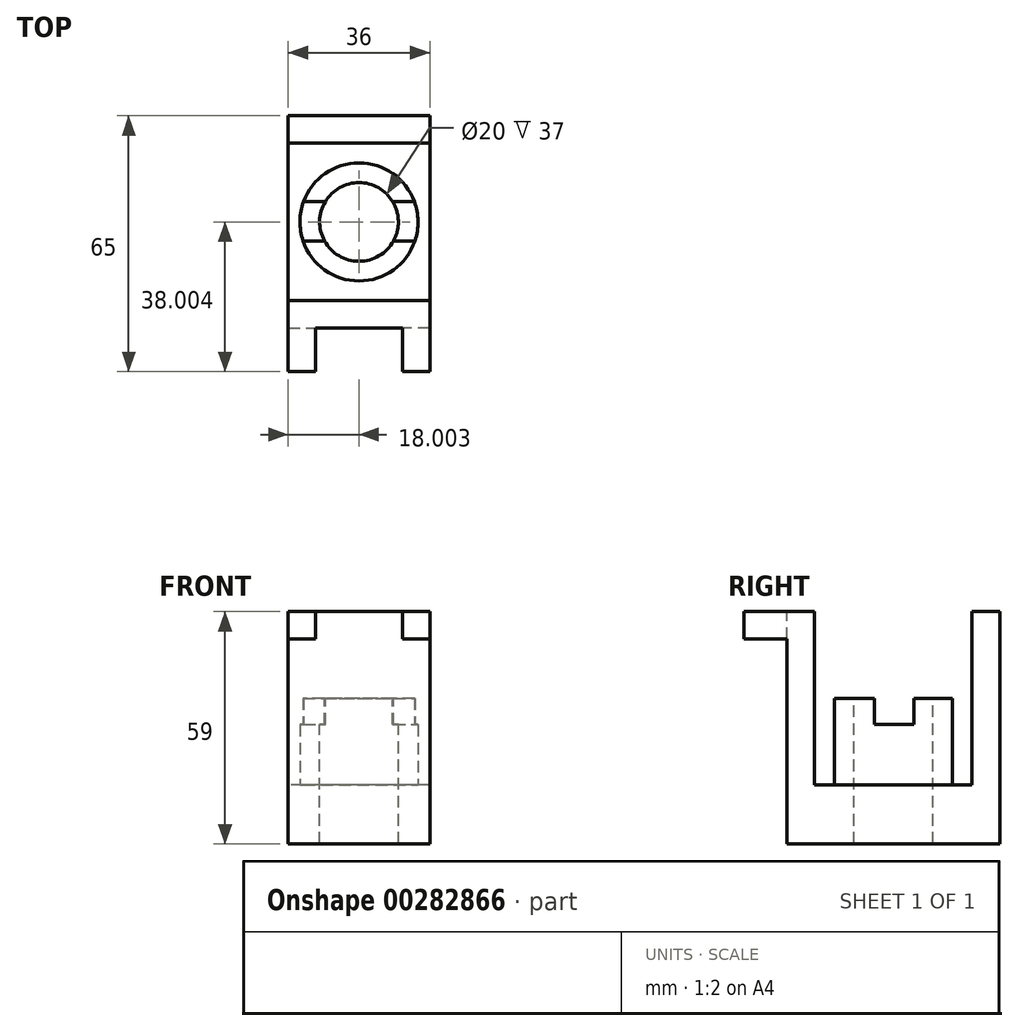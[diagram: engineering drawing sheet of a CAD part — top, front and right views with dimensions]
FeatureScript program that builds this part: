
annotation { "Feature Type Name" : "Feature", "Feature Type Description" : "" }
export const myFeature = defineFeature(function(context is Context, id is Id, definition is map)
    precondition{}
    {
        {
            var Q0;
            Q0=qCreatedBy(makeId("Top.planeOp"),FACE);
            var sketch = newSketch(context, id + "F0", { "sketchPlane" : qUnion([Q0])});
            skLineSegment(sketch, "E0.bottom", {"start": v(-73.88, -73.37) * mm, "end": v(-37.88, -73.37) * mm});
            skLineSegment(sketch, "E0.top", {"start": v(-73.88, -19.37) * mm, "end": v(-37.88, -19.37) * mm});
            skLineSegment(sketch, "E0.left", {"start": v(-73.88, -73.37) * mm, "end": v(-73.88, -19.37) * mm});
            skLineSegment(sketch, "E0.right", {"start": v(-37.88, -73.37) * mm, "end": v(-37.88, -19.37) * mm});
            skSolve(sketch);
        }
        {
            var Q0;
            Q0=makeQuery(id+"F0.imprint","IMPRINT",FACE,{"disambiguationData":[TD([[makeQuery(id+"F0.imprint","IMPRINT",EDGE,{"derivedFrom":sQuery(id+"F0.wireOp",EDGE,"E0.bottom")}),1.0]])]});
            extrude(context, id + "F1", {"entities" : qUnion([Q0]), "depth" : 15 * mm});
        }
        {
            var Q0;
            Q0=makeQuery(id+"F1.opExtrude","CAP_FACE",FACE,{"disambiguationData":[OSD([sQuery(id+"F0.wireOp",EDGE,"E0.bottom"),sQuery(id+"F0.wireOp",EDGE,"E0.top"),sQuery(id+"F0.wireOp",EDGE,"E0.left"),sQuery(id+"F0.wireOp",EDGE,"E0.right")])],"isStart":false});
            var sketch = newSketch(context, id + "F2", { "sketchPlane" : qUnion([Q0])});
            skLineSegment(sketch, "E1.bottom", {"start": v(-73.88, -19.37) * mm, "end": v(-37.88, -19.37) * mm});
            skLineSegment(sketch, "E1.top", {"start": v(-73.88, -26.37) * mm, "end": v(-37.88, -26.37) * mm});
            skLineSegment(sketch, "E1.left", {"start": v(-73.88, -19.37) * mm, "end": v(-73.88, -26.37) * mm});
            skLineSegment(sketch, "E1.right", {"start": v(-37.88, -19.37) * mm, "end": v(-37.88, -26.37) * mm});
            skLineSegment(sketch, "E2.bottom", {"start": v(-37.88, -73.37) * mm, "end": v(-73.88, -73.37) * mm});
            skLineSegment(sketch, "E2.top", {"start": v(-37.88, -66.37) * mm, "end": v(-73.88, -66.37) * mm});
            skLineSegment(sketch, "E2.left", {"start": v(-37.88, -73.37) * mm, "end": v(-37.88, -66.37) * mm});
            skLineSegment(sketch, "E2.right", {"start": v(-73.88, -73.37) * mm, "end": v(-73.88, -66.37) * mm});
            skSolve(sketch);
        }
        {
            var Q0;
            Q0=makeQuery(id+"F2.imprint","IMPRINT",FACE,{"disambiguationData":[TD([[makeQuery(id+"F2.imprint","IMPRINT",EDGE,{"derivedFrom":sQuery(id+"F2.wireOp",EDGE,"E1.bottom")}),-1.0]])]});
            var Q1;
            Q1=makeQuery(id+"F2.imprint","IMPRINT",FACE,{"disambiguationData":[TD([[makeQuery(id+"F2.imprint","IMPRINT",EDGE,{"derivedFrom":sQuery(id+"F2.wireOp",EDGE,"E2.bottom")}),1.0]])]});
            extrude(context, id + "F3", {"entities" : qUnion([Q0, Q1]), "operationType" : NewBodyOperationType.ADD, "depth" : 44 * mm});
        }
        {
            var Q0;
            Q0=makeQuery(id+"F1.opExtrude","CAP_FACE",FACE,{"disambiguationData":[OSD([sQuery(id+"F0.wireOp",EDGE,"E0.bottom"),sQuery(id+"F0.wireOp",EDGE,"E0.top"),sQuery(id+"F0.wireOp",EDGE,"E0.left"),sQuery(id+"F0.wireOp",EDGE,"E0.right")])],"isStart":false});
            var sketch = newSketch(context, id + "F4", { "sketchPlane" : qUnion([Q0])});
            skCircle(sketch, "E3", {"center": v(-55.88, -46.37) * mm, "radius": 15 * mm});
            skPoint(sketch, "E3.centerSnap0", {"position": v(-37.88, -46.37) * mm});
            skPoint(sketch, "E3.centerSnap1", {"position": v(-55.88, -66.37) * mm});
            skSolve(sketch);
        }
        {
            var Q0;
            Q0=makeQuery(id+"F4.imprint","IMPRINT",FACE,{"disambiguationData":[TD([[makeQuery(id+"F4.imprint","IMPRINT",EDGE,{"derivedFrom":sQuery(id+"F4.wireOp",EDGE,"E3")}),1.0]])]});
            extrude(context, id + "F5", {"entities" : qUnion([Q0]), "operationType" : NewBodyOperationType.ADD, "depth" : 22 * mm});
        }
        {
            var Q0;
            Q0=makeQuery(id+"F5.opExtrude","CAP_FACE",FACE,{"disambiguationData":[OSD([sQuery(id+"F4.wireOp",EDGE,"E3")])],"isStart":false});
            var sketch = newSketch(context, id + "F6", { "sketchPlane" : qUnion([Q0])});
            skCircle(sketch, "E4", {"center": v(-55.88, -46.37) * mm, "radius": 10 * mm});
            skSolve(sketch);
        }
        {
            var Q0;
            Q0=sQuery(id+"F6.wireOp",VERTEX,"E4.center");
            var Q1;
            Q1=makeQuery(id+"F1.opExtrude","SWEPT_BODY",BODY,{"disambiguationData":[OSD([sQuery(id+"F0.wireOp",EDGE,"E0.bottom"),sQuery(id+"F0.wireOp",EDGE,"E0.top"),sQuery(id+"F0.wireOp",EDGE,"E0.left"),sQuery(id+"F0.wireOp",EDGE,"E0.right")])]});
            hole(context, id + "F7", {"style" : HoleStyle.SIMPLE, "endStyle" : HoleEndStyle.THROUGH, "holeDiameter" : 20 * mm, "tappedDepth" : 12 * mm, "tapClearance" : 3, "locations" : qUnion([Q0]), "scope" : qUnion([Q1])});
        }
        {
            var Q0;
            Q0=qCreatedBy(makeId("Right.planeOp"),FACE);
            var sketch = newSketch(context, id + "F8", { "sketchPlane" : qUnion([Q0])});
            skLineSegment(sketch, "E5", {"start": v(-61.13, 37.3) * mm, "end": v(-31.23, 37.3) * mm});
            skLineSegment(sketch, "E6", {"start": v(-46.18, 37.3) * mm, "end": v(-46.18, 30.3) * mm});
            skLineSegment(sketch, "E7", {"start": v(-61.13, 37.3) * mm, "end": v(-61.13, 14.8) * mm});
            skLineSegment(sketch, "E8", {"start": v(-61.13, 14.8) * mm, "end": v(-31.23, 14.8) * mm});
            skLineSegment(sketch, "E9", {"start": v(-31.23, 14.8) * mm, "end": v(-31.23, 37.3) * mm});
            skLineSegment(sketch, "E10", {"start": v(-46.18, 30.3) * mm, "end": v(-41.18, 30.3) * mm});
            skLineSegment(sketch, "E11", {"start": v(-46.18, 30.3) * mm, "end": v(-51.18, 30.3) * mm});
            skLineSegment(sketch, "E12", {"start": v(-51.18, 30.3) * mm, "end": v(-51.18, 37.3) * mm});
            skLineSegment(sketch, "E13", {"start": v(-41.18, 30.3) * mm, "end": v(-41.18, 37.3) * mm});
            skSolve(sketch);
        }
        {
            var Q0;
            {var subQ0=sQuery(id+"F8.wireOp",EDGE,"E6");Q0=makeQuery(id+"F8.imprint","IMPRINT",FACE,{"disambiguationData":[TD([[makeQuery(id+"F8.imprint","IMPRINT",EDGE,{"derivedFrom":subQ0}),-1.0]])]});}
            var Q1;
            {var subQ0=sQuery(id+"F8.wireOp",EDGE,"E6");Q1=makeQuery(id+"F8.imprint","IMPRINT",FACE,{"disambiguationData":[TD([[makeQuery(id+"F8.imprint","IMPRINT",EDGE,{"derivedFrom":subQ0}),1.0]])]});}
            extrude(context, id + "F9", {"entities" : qUnion([Q0, Q1]), "operationType" : NewBodyOperationType.REMOVE, "oppositeDirection" : true, "depth" : 9999 * mm});
        }
        {
            var Q0;
            Q0=makeQuery(id+"F3.boolean.opBoolean","MERGE",FACE,{"derivedFrom":[makeQuery(id+"F1.opExtrude","SWEPT_FACE",FACE,{"disambiguationData":[OSD([sQuery(id+"F0.wireOp",EDGE,"E0.bottom")])]}),makeQuery(id+"F3.opExtrude","SWEPT_FACE",FACE,{"disambiguationData":[OSD([sQuery(id+"F2.wireOp",EDGE,"E2.bottom")])]})]});
            var sketch = newSketch(context, id + "F10", { "sketchPlane" : qUnion([Q0])});
            skLineSegment(sketch, "E14", {"start": v(-73.88, 59) * mm, "end": v(-73.88, 52) * mm});
            skLineSegment(sketch, "E15", {"start": v(-37.88, 59) * mm, "end": v(-37.88, 52) * mm});
            skLineSegment(sketch, "E16", {"start": v(-37.88, 52) * mm, "end": v(-44.88, 52) * mm});
            skLineSegment(sketch, "E17", {"start": v(-44.88, 52) * mm, "end": v(-44.88, 59) * mm});
            skLineSegment(sketch, "E18", {"start": v(-73.88, 52) * mm, "end": v(-66.88, 52) * mm});
            skLineSegment(sketch, "E19", {"start": v(-66.88, 52) * mm, "end": v(-66.88, 59) * mm});
            skSolve(sketch);
        }
        {
            var Q0;
            {var subQ0=sQuery(id+"F10.wireOp",EDGE,"E14");Q0=makeQuery(id+"F10.imprint","IMPRINT",FACE,{"disambiguationData":[TD([[makeQuery(id+"F10.imprint","IMPRINT",EDGE,{"derivedFrom":subQ0}),1.0]])]});}
            var Q1;
            {var subQ0=sQuery(id+"F10.wireOp",EDGE,"E15");Q1=makeQuery(id+"F10.imprint","IMPRINT",FACE,{"disambiguationData":[TD([[makeQuery(id+"F10.imprint","IMPRINT",EDGE,{"derivedFrom":subQ0}),-1.0]])]});}
            extrude(context, id + "F11", {"entities" : qUnion([Q0, Q1]), "operationType" : NewBodyOperationType.ADD, "depth" : 11 * mm});
        }
    });
